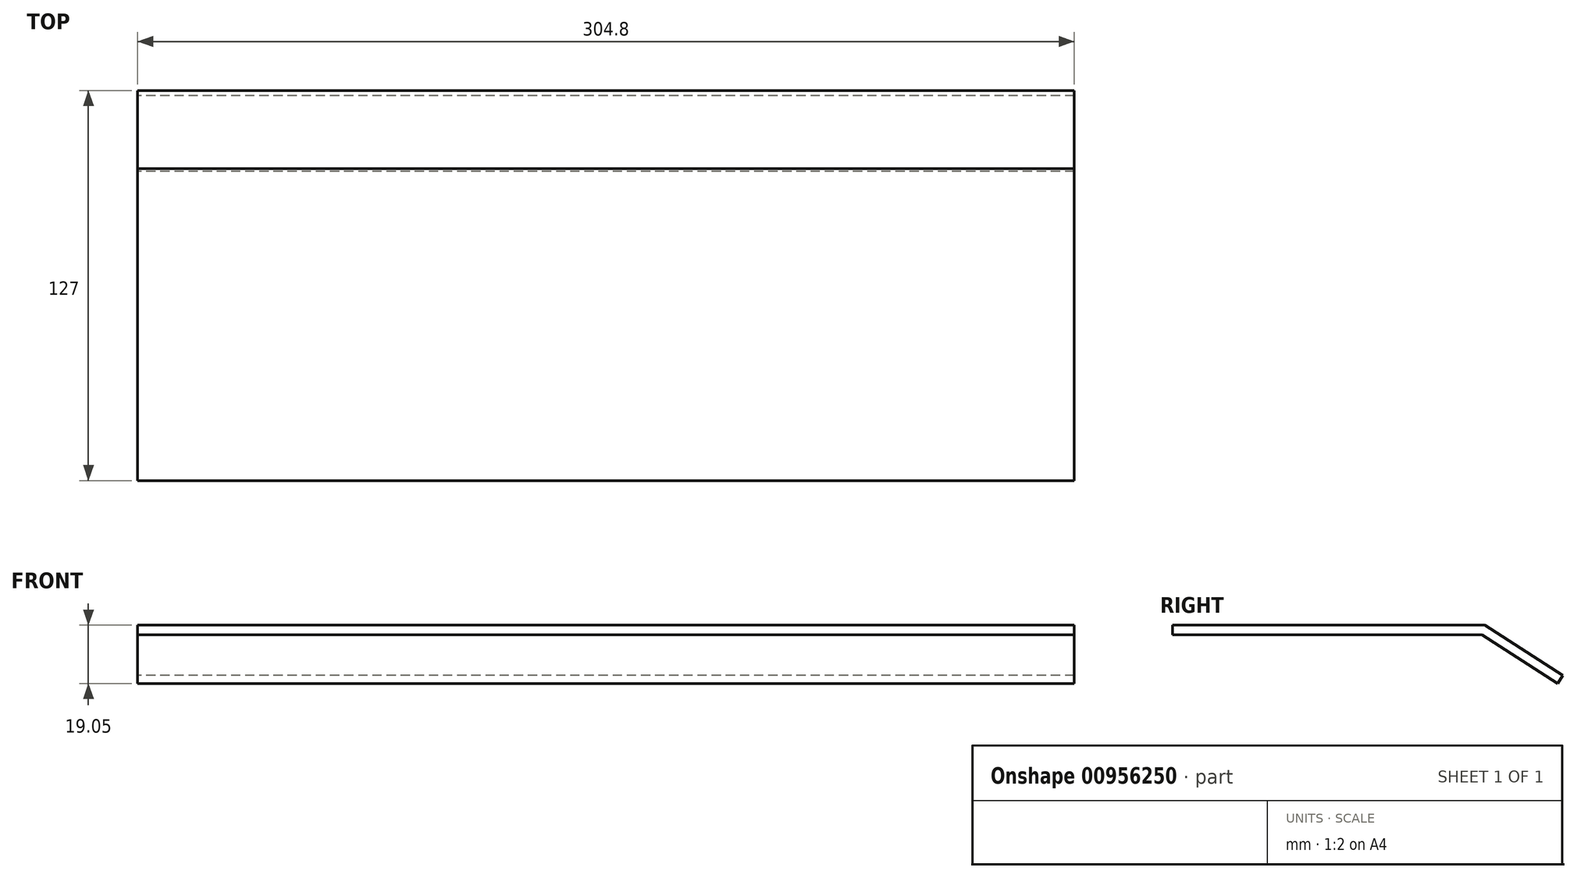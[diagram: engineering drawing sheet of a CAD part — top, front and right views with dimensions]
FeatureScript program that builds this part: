
annotation { "Feature Type Name" : "Feature", "Feature Type Description" : "" }
export const myFeature = defineFeature(function(context is Context, id is Id, definition is map)
    precondition{}
    {
        {
            var Q0;
            Q0=qCreatedBy(makeId("Right.planeOp"),FACE);
            var sketch = newSketch(context, id + "F0", { "sketchPlane" : qUnion([Q0])});
            skLineSegment(sketch, "E0", {"start": v(0, 0) * mm, "end": v(100.66, 0) * mm});
            skLineSegment(sketch, "E1", {"start": v(100.66, 0) * mm, "end": v(125.28, -15.88) * mm});
            skLineSegment(sketch, "E2", {"start": v(125.28, -15.87) * mm, "end": v(127, -13.2) * mm});
            skLineSegment(sketch, "E3", {"start": v(127, -13.2) * mm, "end": v(101.6, 3.18) * mm});
            skLineSegment(sketch, "E4", {"start": v(101.6, 3.17) * mm, "end": v(0, 3.18) * mm});
            skLineSegment(sketch, "E5", {"start": v(0, 3.17) * mm, "end": v(0, 0) * mm});
            skPoint(sketch, "E6.visualSharp", {"position": v(101.6, 3.18) * mm});
            skPoint(sketch, "E7.visualSharp", {"position": v(100.66, 0) * mm});
            skSolve(sketch);
        }
        {
            var Q0;
            Q0 = qSketchRegion(id + "F0", true);
            extrude(context, id + "F1", {"entities" : qUnion([Q0]), "endBound" : BoundingType.SYMMETRIC, "depth" : 304.8 * mm, "offsetDistance" : 25.4 * mm});
        }
    });
